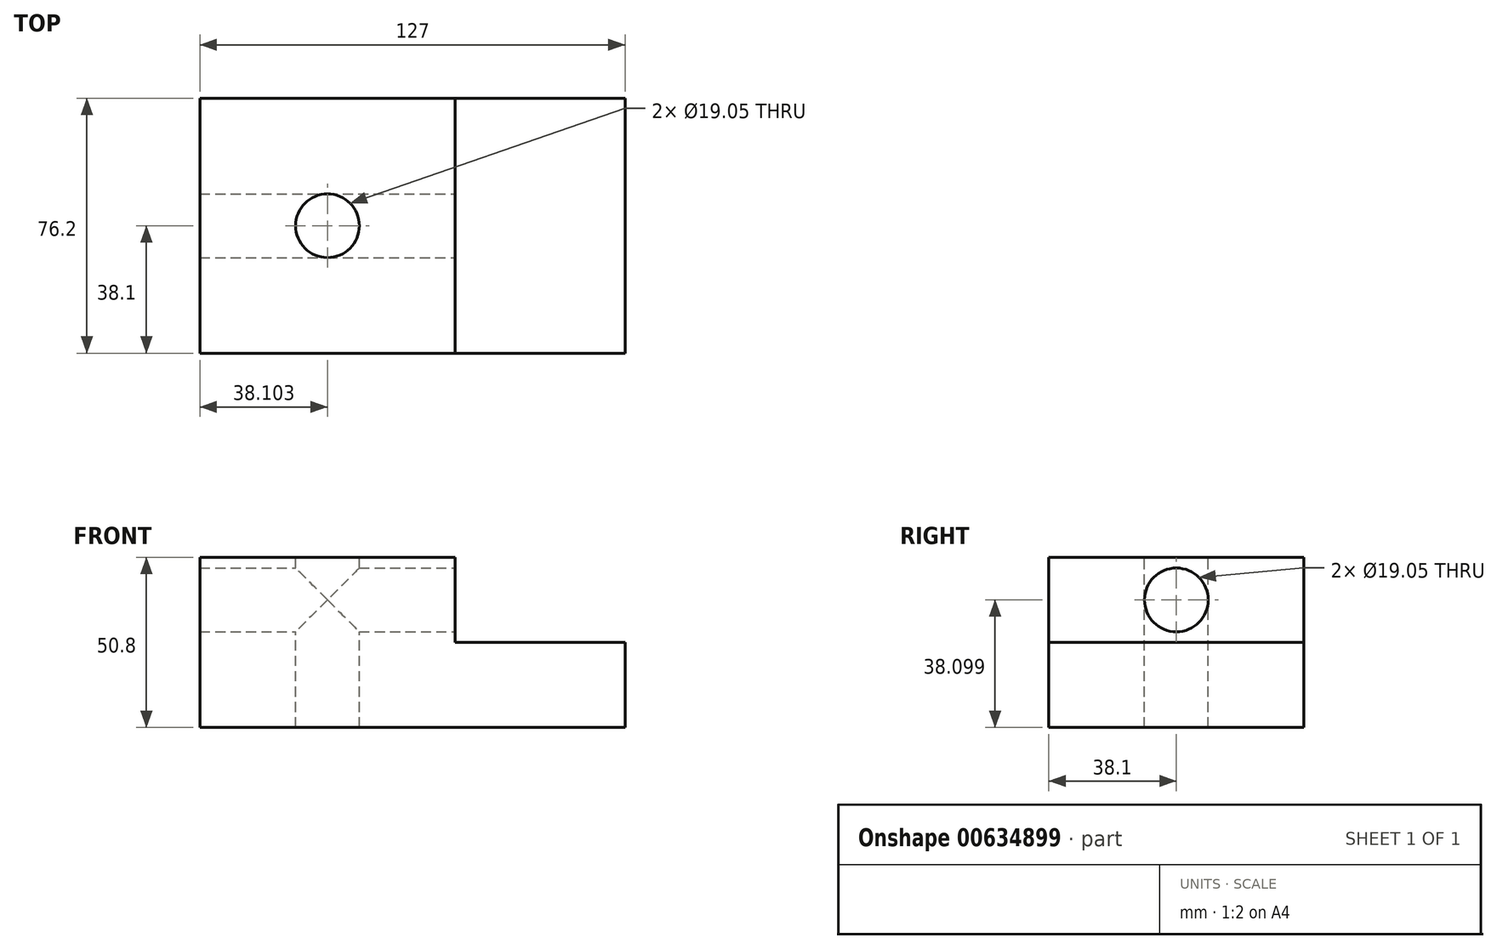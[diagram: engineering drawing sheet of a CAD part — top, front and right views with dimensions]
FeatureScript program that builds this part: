
annotation { "Feature Type Name" : "Feature", "Feature Type Description" : "" }
export const myFeature = defineFeature(function(context is Context, id is Id, definition is map)
    precondition{}
    {
        {
            var Q0;
            Q0=qCreatedBy(makeId("Front.planeOp"),FACE);
            var sketch = newSketch(context, id + "F0", { "sketchPlane" : qUnion([Q0])});
            skLineSegment(sketch, "E0.bottom", {"start": v(-82.22, 55.59) * mm, "end": v(44.78, 55.59) * mm});
            skLineSegment(sketch, "E0.top", {"start": v(-82.22, 4.79) * mm, "end": v(44.78, 4.79) * mm});
            skLineSegment(sketch, "E0.left", {"start": v(-82.22, 55.59) * mm, "end": v(-82.22, 4.79) * mm});
            skLineSegment(sketch, "E0.right", {"start": v(44.78, 55.59) * mm, "end": v(44.78, 4.79) * mm});
            skLineSegment(sketch, "E1", {"start": v(44.78, 30.19) * mm, "end": v(-6.02, 30.19) * mm});
            skLineSegment(sketch, "E2", {"start": v(-6.02, 30.19) * mm, "end": v(-6.02, 55.59) * mm});
            skSolve(sketch);
        }
        {
            var Q0;
            {var subQ1=sQuery(id+"F0.wireOp",EDGE,"E0.top");Q0=makeQuery(id+"F0.imprint","IMPRINT",FACE,{"disambiguationData":[TD([[makeQuery(id+"F0.imprint","IMPRINT",EDGE,{"derivedFrom":subQ1}),1.0]])]});}
            extrude(context, id + "F1", {"entities" : qUnion([Q0]), "depth" : 76.2 * mm, "offsetDistance" : 25.4 * mm});
        }
        {
            var Q0;
            Q0=makeQuery(id+"F1.opExtrude","SWEPT_FACE",FACE,{"disambiguationData":[OSD([sQuery(id+"F0.wireOp",EDGE,"E0.bottom")])]});
            var sketch = newSketch(context, id + "F2", { "sketchPlane" : qUnion([Q0])});
            skPoint(sketch, "E3", {"position": v(-82.22, -38.1) * mm});
            skPoint(sketch, "E4", {"position": v(-44.12, -76.2) * mm});
            skPoint(sketch, "E5", {"position": v(-44.12, -38.1) * mm});
            skSolve(sketch);
        }
        {
            var Q0;
            Q0=sQuery(id+"F2.wireOp",VERTEX,"E5");
            var Q1;
            Q1=makeQuery(id+"F1.opExtrude","SWEPT_BODY",BODY,{"disambiguationData":[OSD([sQuery(id+"F0.wireOp",EDGE,"E0.bottom"),sQuery(id+"F0.wireOp",EDGE,"E0.top"),sQuery(id+"F0.wireOp",EDGE,"E0.left"),sQuery(id+"F0.wireOp",EDGE,"E0.right"),sQuery(id+"F0.wireOp",EDGE,"E1"),sQuery(id+"F0.wireOp",EDGE,"E2")])]});
            hole(context, id + "F3", {"style" : HoleStyle.SIMPLE, "endStyle" : HoleEndStyle.THROUGH, "holeDiameter" : 19.05 * mm, "majorDiameter" : 6.35 * mm, "isTappedThrough" : true, "tappedDepth" : 12.7 * mm, "tapClearance" : 3, "locations" : qUnion([Q0]), "scope" : qUnion([Q1])});
        }
        {
            var Q0;
            Q0=makeQuery(id+"F1.opExtrude","SWEPT_FACE",FACE,{"disambiguationData":[OSD([sQuery(id+"F0.wireOp",EDGE,"E2")])]});
            var sketch = newSketch(context, id + "F4", { "sketchPlane" : qUnion([Q0])});
            skPoint(sketch, "E6", {"position": v(-76.2, 42.89) * mm});
            skPoint(sketch, "E7", {"position": v(-38.1, 30.19) * mm});
            skPoint(sketch, "E8", {"position": v(-38.1, 42.89) * mm});
            skSolve(sketch);
        }
        {
            var Q0;
            Q0=sQuery(id+"F4.wireOp",VERTEX,"E8");
            var Q1;
            Q1=makeQuery(id+"F1.opExtrude","SWEPT_BODY",BODY,{"disambiguationData":[OSD([sQuery(id+"F0.wireOp",EDGE,"E0.bottom"),sQuery(id+"F0.wireOp",EDGE,"E0.top"),sQuery(id+"F0.wireOp",EDGE,"E0.left"),sQuery(id+"F0.wireOp",EDGE,"E0.right"),sQuery(id+"F0.wireOp",EDGE,"E1"),sQuery(id+"F0.wireOp",EDGE,"E2")])]});
            hole(context, id + "F5", {"style" : HoleStyle.SIMPLE, "endStyle" : HoleEndStyle.THROUGH, "holeDiameter" : 19.05 * mm, "majorDiameter" : 6.35 * mm, "isTappedThrough" : true, "tappedDepth" : 12.7 * mm, "tapClearance" : 3, "locations" : qUnion([Q0]), "scope" : qUnion([Q1])});
        }
    });
